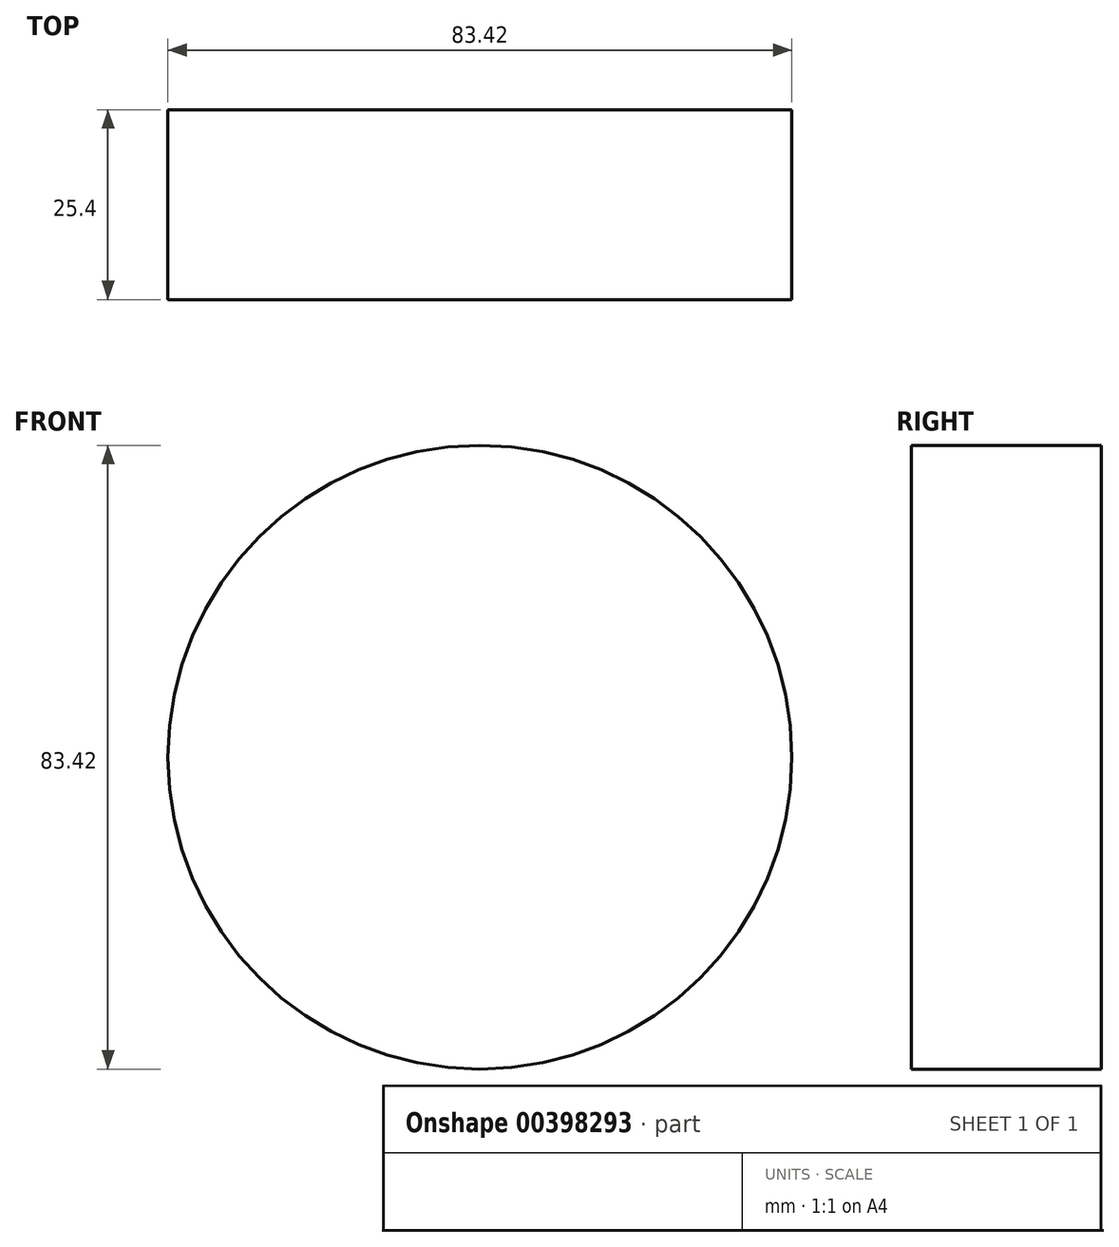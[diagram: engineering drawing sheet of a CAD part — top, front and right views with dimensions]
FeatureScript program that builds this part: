
annotation { "Feature Type Name" : "Feature", "Feature Type Description" : "" }
export const myFeature = defineFeature(function(context is Context, id is Id, definition is map)
    precondition{}
    {
        {
            var Q0;
            Q0=qCreatedBy(makeId("Front.planeOp"),FACE);
            var sketch = newSketch(context, id + "F0", { "sketchPlane" : qUnion([Q0])});
            skCircle(sketch, "E0", {"center": v(0, 0) * mm, "radius": 41.95 * mm});
            skCircle(sketch, "E1", {"center": v(0, 0) * mm, "radius": 41.71 * mm});
            skCircle(sketch, "E2", {"center": v(0, 0) * mm, "radius": 41.81 * mm});
            skSolve(sketch);
        }
        {
            var Q0;
            Q0=makeQuery(id+"F0.imprint","IMPRINT",FACE,{"disambiguationData":[TD([[makeQuery(id+"F0.imprint","IMPRINT",EDGE,{"derivedFrom":sQuery(id+"F0.wireOp",EDGE,"E1")}),1.0]])]});
            extrude(context, id + "F1", {"entities" : qUnion([Q0]), "depth" : 25.4 * mm});
        }
    });
